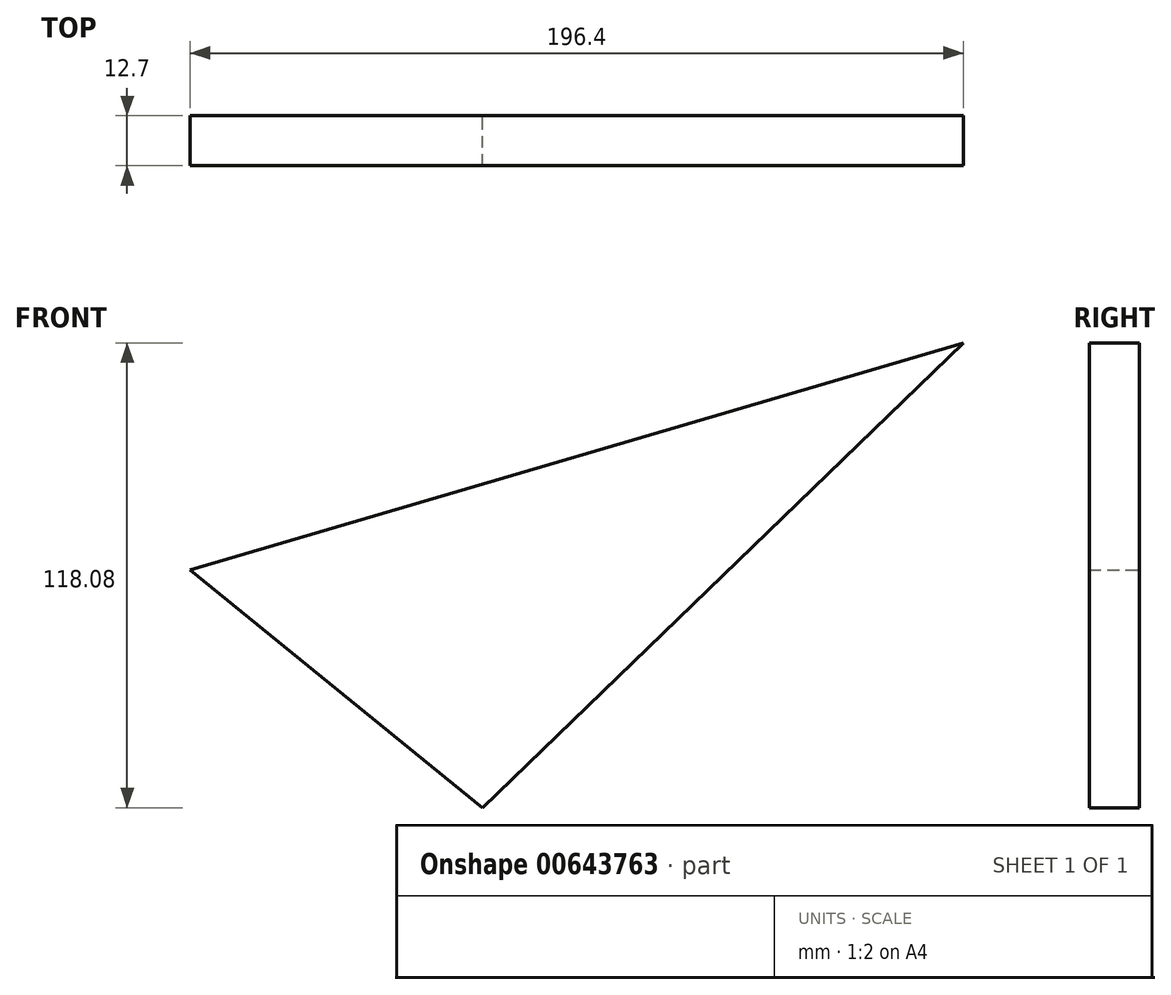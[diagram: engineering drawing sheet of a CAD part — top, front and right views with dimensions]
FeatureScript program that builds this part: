
annotation { "Feature Type Name" : "Feature", "Feature Type Description" : "" }
export const myFeature = defineFeature(function(context is Context, id is Id, definition is map)
    precondition{}
    {
        {
            var Q0;
            Q0=qCreatedBy(makeId("Front.planeOp"),FACE);
            var sketch = newSketch(context, id + "F0", { "sketchPlane" : qUnion([Q0])});
            skLineSegment(sketch, "E0", {"start": v(-74.29, 60.36) * mm, "end": v(0, 0) * mm});
            skLineSegment(sketch, "E1", {"start": v(0, 0) * mm, "end": v(122.1, 118.08) * mm});
            skLineSegment(sketch, "E2", {"start": v(122.1, 118.08) * mm, "end": v(-74.29, 60.36) * mm});
            skSolve(sketch);
        }
        {
            var Q0;
            Q0 = qSketchRegion(id + "F0", true);
            extrude(context, id + "F1", {"entities" : qUnion([Q0]), "depth" : 12.7 * mm, "offsetDistance" : 25.4 * mm});
        }
    });
